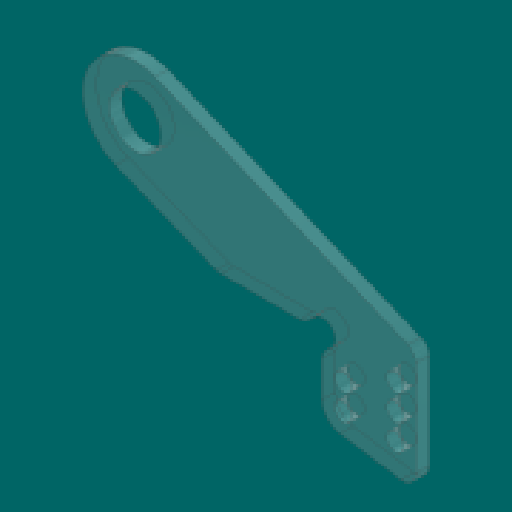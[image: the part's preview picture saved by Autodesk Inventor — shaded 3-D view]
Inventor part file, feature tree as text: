
AUTODESK INVENTOR PART (.ipt)
format: ipt  version: 2023.1 (Build 271208000, 208)  size: 137,216 bytes
history: native  units: in
note: dims shown in document units (in); Inventor stores cm internally (conversion verified against a paired STEP export)
features: other x3, extrude x1, fillet x1, sketch x1, reference x1
ambient origin geometry x8: Origin, YZ Plane, XZ Plane, XY Plane, X Axis, Y Axis, Z Axis, Center Point
bodies: Solid1 (feature_tree)
feature tree (7):
  extrude  "Extrusion1"  Depth=0.125in
  fillet  "Fillet1"  Radius=4.5in
  sketch  "Sketch1"  dims[d3=0.5in d4=2.0in d5=4.5in d6=1.8in d8=1.0in d10=0.25in d12=0.06in d13=1.0in d14=0.125in d15=0.0in d16=0.125in]
  reference  "Reference1"
  other  "<userpath>\Documents\CAD\spin-up-18_1\MainAssy.iam"
  other  "MainAssy.iam"
  other  "IntakeArm:2"
